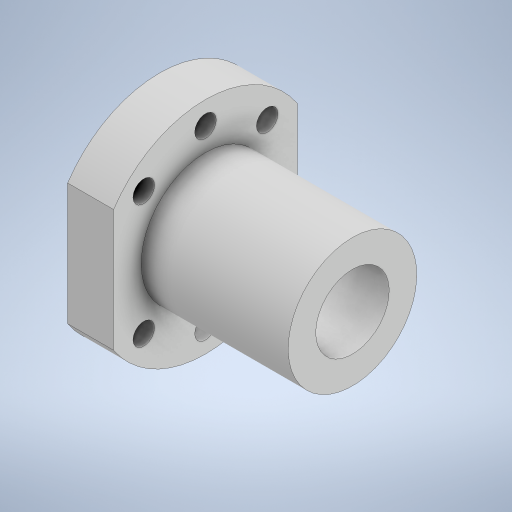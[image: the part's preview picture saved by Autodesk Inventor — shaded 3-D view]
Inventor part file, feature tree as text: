
AUTODESK INVENTOR PART (.ipt)
format: ipt  version: 2023 (Build 270158000, 158)  size: 274,432 bytes
history: native  units: mm
features: sketch x2, revolve x1, extrude x1
ambient origin geometry x8: Origin, YZ Plane, XZ Plane, XY Plane, X Axis, Y Axis, Z Axis, Center Point
bodies: Solid1 (feature_tree)
feature tree (4):
  revolve  "Revolution1"  [1 undecoded]
  extrude  "Extrusion1"  Depth=10.0mm
  sketch  "Sketch1"  dims[d0=8.0mm d1=14.0mm]
  sketch  "Sketch2"  dims[d2=24.0mm d3=10.0mm d4=42.0mm d5=90.0deg d6=38.0mm d7=40.0mm d8=4.7mm d9=45.0deg d10=10.0mm d11=0.0mm]
note: 1 required parameter value undecoded (feature->parameter linkage not recoverable at this tier; creation-order binding heuristic only, values carry confidence <= 0.55)
